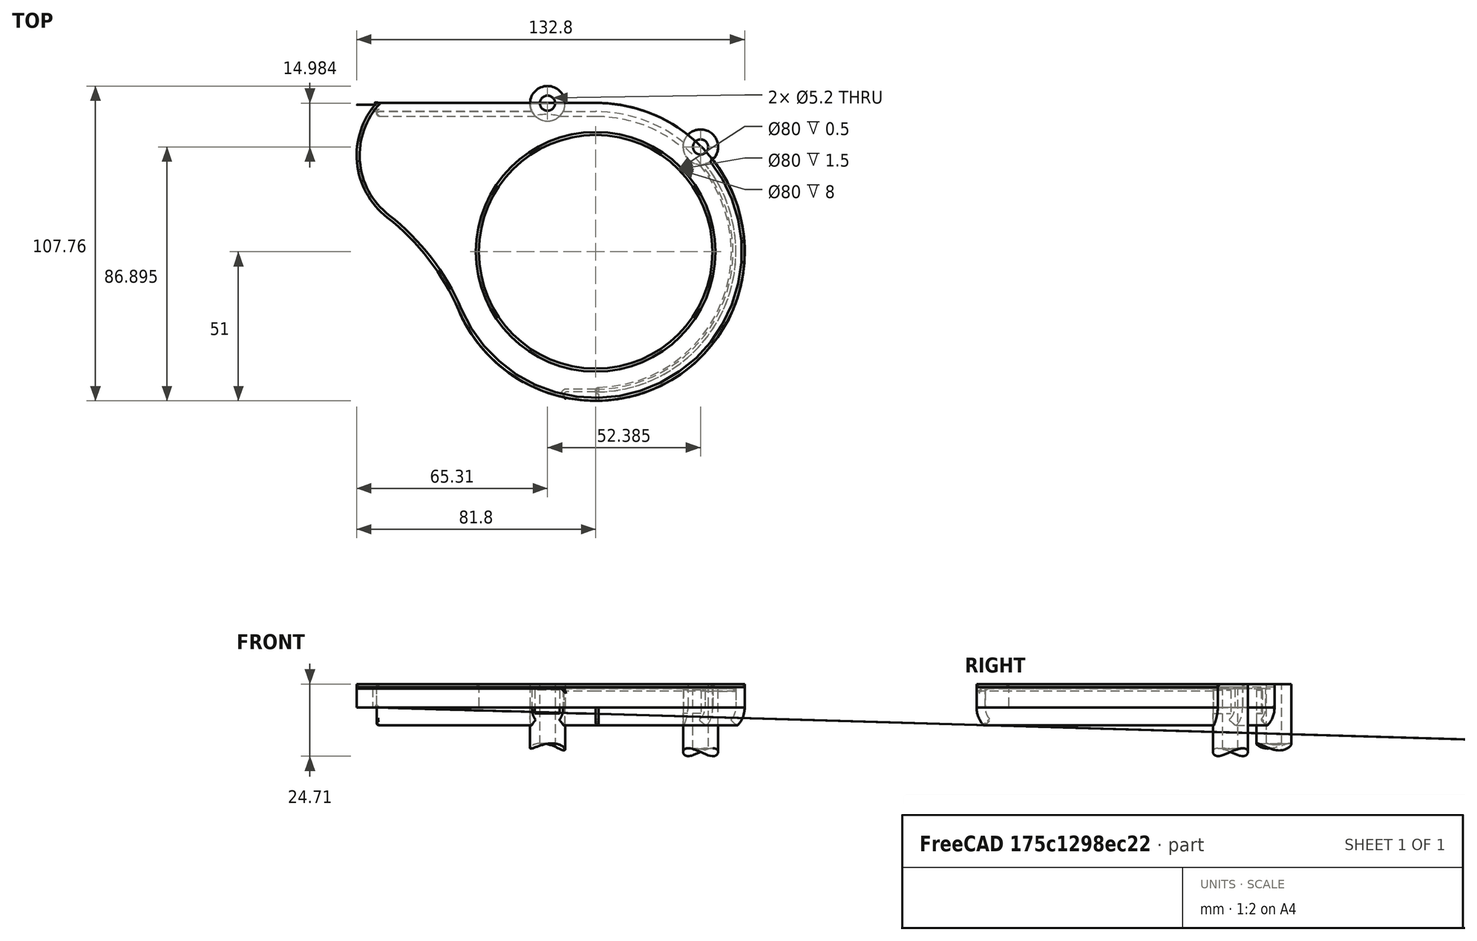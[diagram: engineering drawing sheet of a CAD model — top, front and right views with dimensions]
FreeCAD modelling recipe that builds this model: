
FCSTD DOCUMENT  (FreeCAD 0.16R)
Label: SimpleChainguard5
License: All rights reserved
LicenseURL: http://en.wikipedia.org/wiki/All_rights_reserved
objects: Sketcher::SketchObject×6, Part::Cylinder×4, PartDesign::Pad×3, Part::Cut×3, PartDesign::Chamfer×3, PartDesign::Pocket×2, Part::MultiFuse×2, PartDesign::Fillet×2, PartDesign::Revolution×1, Mesh::Feature×1
note: 32 computed .brp shape members not serialized (recipe doc carries the construction recipe); baked Part::Feature solids carry a one-line shape summary decoded from their .brp

FEATURE [Sketcher::SketchObject] Sketch
  sketch-geometry (7):
    g0: Circle CenterX=0 CenterY=0 CenterZ=0 NormalX=0 NormalY=0 NormalZ=1 Radius=40
    g1: ArcOfCircle CenterX=0 CenterY=0 CenterZ=0 NormalX=0 NormalY=0 NormalZ=1 Radius=51 StartAngle=3.54457 EndAngle=7.85398
    g2: LineSegment StartX=-75 StartY=51 StartZ=0 EndX=0 EndY=51 EndZ=0
    g3: ArcOfCircle CenterX=-54.8043 CenterY=33.0798 CenterZ=0 NormalX=0 NormalY=0 NormalZ=1 Radius=27 StartAngle=2.41582 EndAngle=4.05122
    g4: ArcOfCircle CenterX=-120.507 CenterY=-51.3726 CenterZ=0 NormalX=0 NormalY=0 NormalZ=1 Radius=80 StartAngle=0.402976 EndAngle=0.909627
    g5: LineSegment [constr] StartX=0 StartY=0 StartZ=0 EndX=114.907 EndY=96.4181 EndZ=0
    g6: LineSegment [constr] StartX=-46.3525 StartY=142.658 StartZ=0 EndX=0 EndY=0 EndZ=0
  constraints (22):
    c: Radius(g0) = 40
    c: Coincident(g0,g-1)
    c: Coincident(g1,g-1)
    c: PointOnObject(g1,g-2)
    c: Coincident(g2,g1)
    c: Horizontal(g2)
    c: Distance(g2) = 75
    c: Coincident(g3,g2)
    c: Coincident(g4,g3)
    c: Coincident(g4,g1)
    c: Tangent(g4,g3)
    c: Tangent(g1,g4)
    c: Radius(g1) = 51
    c: Radius(g4) = 80
    c: Radius(g3) = 27
    c: Coincident(g5,g-1)
    c: Angle(g6) = -1.25664
    c: Coincident(g6,g-1)
    c: Angle(g5) = 0.698132
    c: Distance(g5) = 150
    c: Distance(g6) = 150
    c: DistanceY(g1) = -20
FEATURE [PartDesign::Pad] Pad
  Length = 8
  Length2 = 100
  Sketch = -> Sketch
  Type = 0
FEATURE [Sketcher::SketchObject] Sketch001
  ExternalGeometry = -> [Pad]
  Placement = pos=(0,0,0) rot=(1,0,0;3.14159rad)
  Support = -> Pad [Face6]
  sketch-geometry (4):
    g0: LineSegment StartX=-146.216 StartY=-48 StartZ=0 EndX=0 EndY=-48 EndZ=0
    g1: ArcOfCircle CenterX=0 CenterY=0 CenterZ=0 NormalX=0 NormalY=0 NormalZ=1 Radius=48 StartAngle=4.71239 EndAngle=7.85398
    g2: LineSegment StartX=0 StartY=48 StartZ=0 EndX=-146.216 EndY=48 EndZ=0
    g3: LineSegment StartX=-146.216 StartY=-48 StartZ=0 EndX=-146.216 EndY=48 EndZ=0
  constraints (12):
    c: Coincident(g1,g-1)
    c: PointOnObject(g1,g-2)
    c: Coincident(g2,g1)
    c: Horizontal(g2)
    c: Coincident(g3,g0)
    c: Coincident(g3,g2)
    c: Vertical(g3)
    c: Distance(g2) = 146.216
    c: Coincident(g0,g1)
    c: PointOnObject(g0,g-2)
    c: Distance(g-4,g0) = 3
    c: Horizontal(g0)
FEATURE [PartDesign::Pocket] Pocket
  Length = 6.5
  Sketch = -> Sketch001
  Type = 0
FEATURE [Sketcher::SketchObject] Sketch004
  Placement = pos=(0,0,0) rot=(0.57735,0.57735,0.57735;2.0944rad)
  sketch-geometry (6):
    g0: LineSegment StartX=48.3639 StartY=-6.36399 StartZ=0 EndX=46.2426 EndY=-4.24266 EndZ=0
    g1: ArcOfCircle CenterX=42 CenterY=0 CenterZ=0 NormalX=0 NormalY=0 NormalZ=1 Radius=6 StartAngle=5.49778 EndAngle=6.28319
    g2: ArcOfCircle CenterX=42 CenterY=0 CenterZ=0 NormalX=0 NormalY=0 NormalZ=1 Radius=9 StartAngle=5.49778 EndAngle=6.28319
    g3: LineSegment [constr] StartX=35.4204 StartY=-19.3075 StartZ=0 EndX=48.3639 EndY=-6.36399 EndZ=0
    g4: LineSegment [constr] StartX=20.3373 StartY=-30.148 StartZ=0 EndX=46.2426 EndY=-4.24266 EndZ=0
    g5: LineSegment StartX=48 StartY=0 StartZ=0 EndX=51 EndY=0 EndZ=0
  constraints (19):
    c: Coincident(g2,g1)
    c: Parallel(g3,g4)
    c: Angle(g4) = 0.785398
    c: Coincident(g0,g2)
    c: Coincident(g0,g1)
    c: Coincident(g5,g1)
    c: Coincident(g5,g2)
    c: Perpendicular(g2,g0)
    c: DistanceX(g1) = 42
    c: Distance(g3) = 18.3049
    c: Distance(g4) = 36.6357
    c: Distance(g5) = 3
    c: Coincident(g0,g3)
    c: Coincident(g4,g0)
    c: Tangent(g4,g1)
    c: Horizontal(g5)
    c: Perpendicular(g2,g5)
    c: DistanceX(g2) = 51
    c: PointOnObject(g2,g-1)
FEATURE [PartDesign::Revolution] Revolution
  Angle = 180
  Axis = (0,0,1)
  Base = (0,0,0)
  Placement = pos=(0,0,0) rot=(0.57735,0.57735,0.57735;2.0944rad)
  ReferenceAxis = -> Sketch004 [V_Axis]
  Reversed = true
  Sketch = -> Sketch004
FEATURE [Sketcher::SketchObject] Sketch005
  sketch-geometry (4):
    g0: LineSegment [constr] StartX=-45.1089 StartY=138.831 StartZ=0 EndX=0 EndY=0 EndZ=0
    g1: LineSegment [constr] StartX=122.75 StartY=122.75 StartZ=0 EndX=0 EndY=0 EndZ=0
    g2: Circle CenterX=-16.4924 CenterY=50.7583 CenterZ=0 NormalX=0 NormalY=0 NormalZ=1 Radius=6
    g3: Circle CenterX=35.8947 CenterY=35.8947 CenterZ=0 NormalX=0 NormalY=0 NormalZ=1 Radius=6
  constraints (8):
    c: Coincident(g0,g-1)
    c: Coincident(g1,g-1)
    c: Angle(g1) = -2.35619
    c: Angle(g0) = -1.25664
    c: Radius(g2) = 6
    c: PointOnObject(g2,g0)
    c: Radius(g3) = 6
    c: PointOnObject(g3,g1)
FEATURE [PartDesign::Pad] Pad001
  Length = 8
  Length2 = 25
  Sketch = -> Sketch005
  Type = 4
FEATURE [Sketcher::SketchObject] Sketch006
  Placement = pos=(0,0,0) rot=(0.57735,0.57735,0.57735;2.0944rad)
  sketch-geometry (6):
    g0: LineSegment StartX=48.3639 StartY=-6.36399 StartZ=0 EndX=46.2426 EndY=-4.24266 EndZ=0
    g1: ArcOfCircle CenterX=42 CenterY=0 CenterZ=0 NormalX=0 NormalY=0 NormalZ=1 Radius=6 StartAngle=5.49778 EndAngle=6.28319
    g2: ArcOfCircle CenterX=42 CenterY=0 CenterZ=0 NormalX=0 NormalY=0 NormalZ=1 Radius=9 StartAngle=5.49778 EndAngle=6.28319
    g3: LineSegment [constr] StartX=35.4204 StartY=-19.3075 StartZ=0 EndX=48.3639 EndY=-6.36399 EndZ=0
    g4: LineSegment [constr] StartX=20.3373 StartY=-30.148 StartZ=0 EndX=46.2426 EndY=-4.24266 EndZ=0
    g5: LineSegment StartX=48 StartY=0 StartZ=0 EndX=51 EndY=0 EndZ=0
  constraints (19):
    c: Coincident(g2,g1)
    c: Parallel(g3,g4)
    c: Angle(g4) = 0.785398
    c: Coincident(g0,g2)
    c: Coincident(g0,g1)
    c: Coincident(g5,g1)
    c: Coincident(g5,g2)
    c: Perpendicular(g2,g0)
    c: DistanceX(g1) = 42
    c: Distance(g3) = 18.3049
    c: Distance(g4) = 36.6357
    c: Distance(g5) = 3
    c: Coincident(g0,g3)
    c: Coincident(g4,g0)
    c: Tangent(g4,g1)
    c: Horizontal(g5)
    c: Perpendicular(g2,g5)
    c: DistanceX(g2) = 51
    c: PointOnObject(g2,g-1)
FEATURE [PartDesign::Pad] Pad002
  Length = 75
  Length2 = 100
  Placement = pos=(0,0,0) rot=(0.57735,0.57735,0.57735;2.0944rad)
  Reversed = true
  Sketch = -> Sketch006
  Type = 0
FEATURE [Part::Cylinder] Cylinder
  Angle = 360
  Height = 100
  Placement = pos=(0,0,-22) rot=(-0.948683,-0.316228,0;1.5708rad)
  Radius = 9.7
FEATURE [Part::Cylinder] Cylinder001
  Angle = 360
  Height = 100
  Placement = pos=(0,0,-22) rot=(-0.707107,0.707107,0;1.5708rad)
  Radius = 8
FEATURE [Part::MultiFuse] Fusion
  Shapes = -> [Pocket,Revolution,Pad001,Pad002]
FEATURE [Part::MultiFuse] Fusion001
  Shapes = -> [Cylinder001,Cylinder]
FEATURE [Part::Cut] Cut
  Base = -> Fusion
  Tool = -> Fusion001
FEATURE [PartDesign::Fillet] Fillet
  Base = -> Cut [Edge27,Edge17,Edge91,Edge87,Edge75,Edge77]
  Radius = 1
FEATURE [PartDesign::Fillet] Fillet001
  Base = -> Fillet [Edge79,Edge77,Edge93,Edge91,Edge105,Edge97,Edge110,Edge107]
  Radius = 0.5
FEATURE [Sketcher::SketchObject] Sketch007
  ExternalGeometry = -> [Fillet001]
  Placement = pos=(0,0,8) rot=(0,0,1;0rad)
  Support = -> Fillet001 [Face48]
  sketch-geometry (2):
    g0: Circle CenterX=35.8947 CenterY=35.8947 CenterZ=0 NormalX=0 NormalY=0 NormalZ=1 Radius=2.6
    g1: Circle CenterX=-16.4899 CenterY=50.8791 CenterZ=0 NormalX=0 NormalY=0 NormalZ=1 Radius=2.6
  constraints (4):
    c: Radius(g1) = 2.6
    c: Equal(g1,g0)
    c: Symmetric(g-4,g-4,g1)
    c: Coincident(g0,g-6)
FEATURE [PartDesign::Pocket] Pocket001
  Length = 5
  Sketch = -> Sketch007
  Type = 1
FEATURE [Part::Cylinder] Cylinder002
  Angle = 360
  Height = 8
  Placement = pos=(-17,27,-2) rot=(0,0,1;0rad)
  Radius = 20
FEATURE [Part::Cylinder] Cylinder003
  Angle = 360
  Height = 8
  Placement = pos=(12,12,-2) rot=(0,0,1;0rad)
  Radius = 30
FEATURE [Part::Cut] Cut001
  Base = -> Pocket001
  Tool = -> Cylinder003
FEATURE [Part::Cut] Cut002
  Base = -> Cut001
  Tool = -> Cylinder002
FEATURE [PartDesign::Chamfer] Chamfer
  Base = -> Cut002 [Edge127]
  Size = 1
FEATURE [PartDesign::Chamfer] Chamfer001
  Base = -> Chamfer [Edge28]
  Size = 1
FEATURE [PartDesign::Chamfer] Chamfer002
  Base = -> Chamfer001 [Edge120]
  Size = 1
FEATURE [Mesh::Feature] Mesh  label="Chamfer002 (Meshed)"
